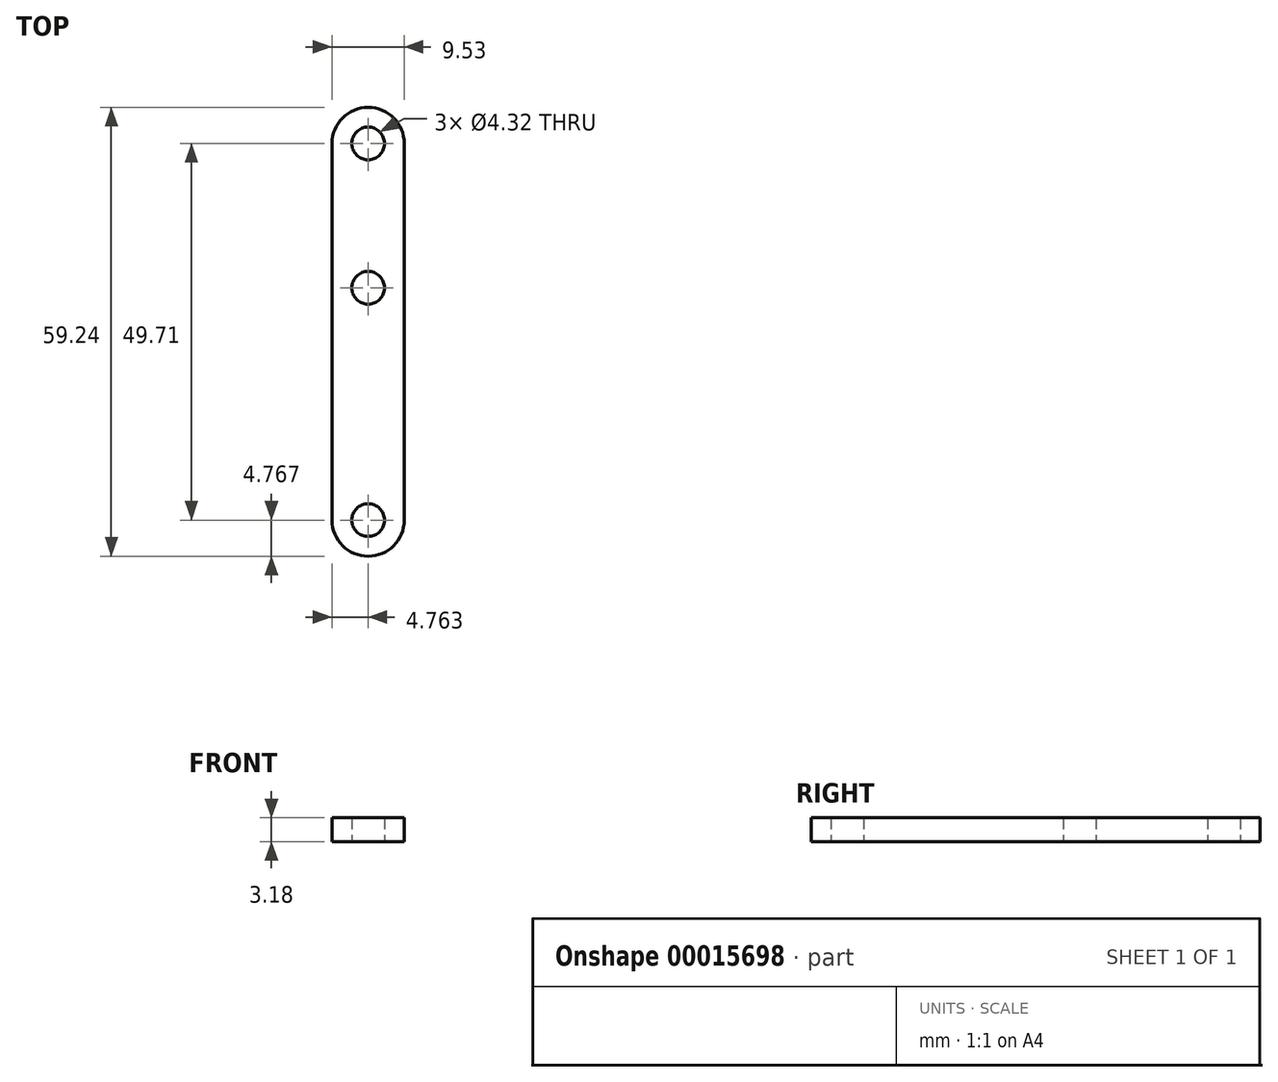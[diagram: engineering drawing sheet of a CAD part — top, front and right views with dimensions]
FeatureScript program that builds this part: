
annotation { "Feature Type Name" : "Feature", "Feature Type Description" : "" }
export const myFeature = defineFeature(function(context is Context, id is Id, definition is map)
    precondition{}
    {
        {
            var Q0;
            Q0=qCreatedBy(makeId("Top.planeOp"),FACE);
            var sketch = newSketch(context, id + "F0", { "sketchPlane" : qUnion([Q0])});
            skLineSegment(sketch, "E0.bottom", {"start": v(0, 0) * mm, "end": v(9.53, 0) * mm});
            skLineSegment(sketch, "E0.top", {"start": v(0, -59.24) * mm, "end": v(9.53, -59.24) * mm});
            skLineSegment(sketch, "E0.left", {"start": v(0, 0) * mm, "end": v(0, -59.24) * mm});
            skLineSegment(sketch, "E0.right", {"start": v(9.53, 0) * mm, "end": v(9.53, -59.24) * mm});
            skLineSegment(sketch, "E1", {"start": v(4.76, 0) * mm, "end": v(4.76, -4.76) * mm, "construction": true});
            skLineSegment(sketch, "E2", {"start": v(4.76, -4.76) * mm, "end": v(4.76, -23.81) * mm, "construction": true});
            skCircle(sketch, "E3", {"center": v(4.76, -4.76) * mm, "radius": 2.16 * mm});
            skCircle(sketch, "E4", {"center": v(4.76, -23.81) * mm, "radius": 2.16 * mm});
            skLineSegment(sketch, "E5", {"start": v(4.76, -59.24) * mm, "end": v(4.76, -54.47) * mm, "construction": true});
            skCircle(sketch, "E6", {"center": v(4.76, -54.47) * mm, "radius": 2.16 * mm});
            skSolve(sketch);
        }
        {
            var Q0;
            Q0 = qSketchRegion(id + "F0", true);
            extrude(context, id + "F1", {"entities" : qUnion([Q0]), "depth" : 3.17 * mm});
        }
        {
            var Q0;
            Q0=makeQuery(id+"F1.opExtrude","SWEPT_EDGE",EDGE,{"disambiguationData":[OSD([sQuery(id+"F0.wireOp",EDGE,"E0.top"),sQuery(id+"F0.wireOp",EDGE,"E0.right")])]});
            var Q1;
            Q1=makeQuery(id+"F1.opExtrude","SWEPT_EDGE",EDGE,{"disambiguationData":[OSD([sQuery(id+"F0.wireOp",EDGE,"E0.top"),sQuery(id+"F0.wireOp",EDGE,"E0.left")])]});
            var Q2;
            Q2=makeQuery(id+"F1.opExtrude","SWEPT_EDGE",EDGE,{"disambiguationData":[OSD([sQuery(id+"F0.wireOp",EDGE,"E0.bottom"),sQuery(id+"F0.wireOp",EDGE,"E0.left")])]});
            var Q3;
            Q3=makeQuery(id+"F1.opExtrude","SWEPT_EDGE",EDGE,{"disambiguationData":[OSD([sQuery(id+"F0.wireOp",EDGE,"E0.bottom"),sQuery(id+"F0.wireOp",EDGE,"E0.right")])]});
            fillet(context, id + "F2", {"entities" : qUnion([Q0, Q1, Q2, Q3]), "radius" : 4.76 * mm, "tangentPropagation" : true, "allowEdgeOverflow" : false});
        }
    });
